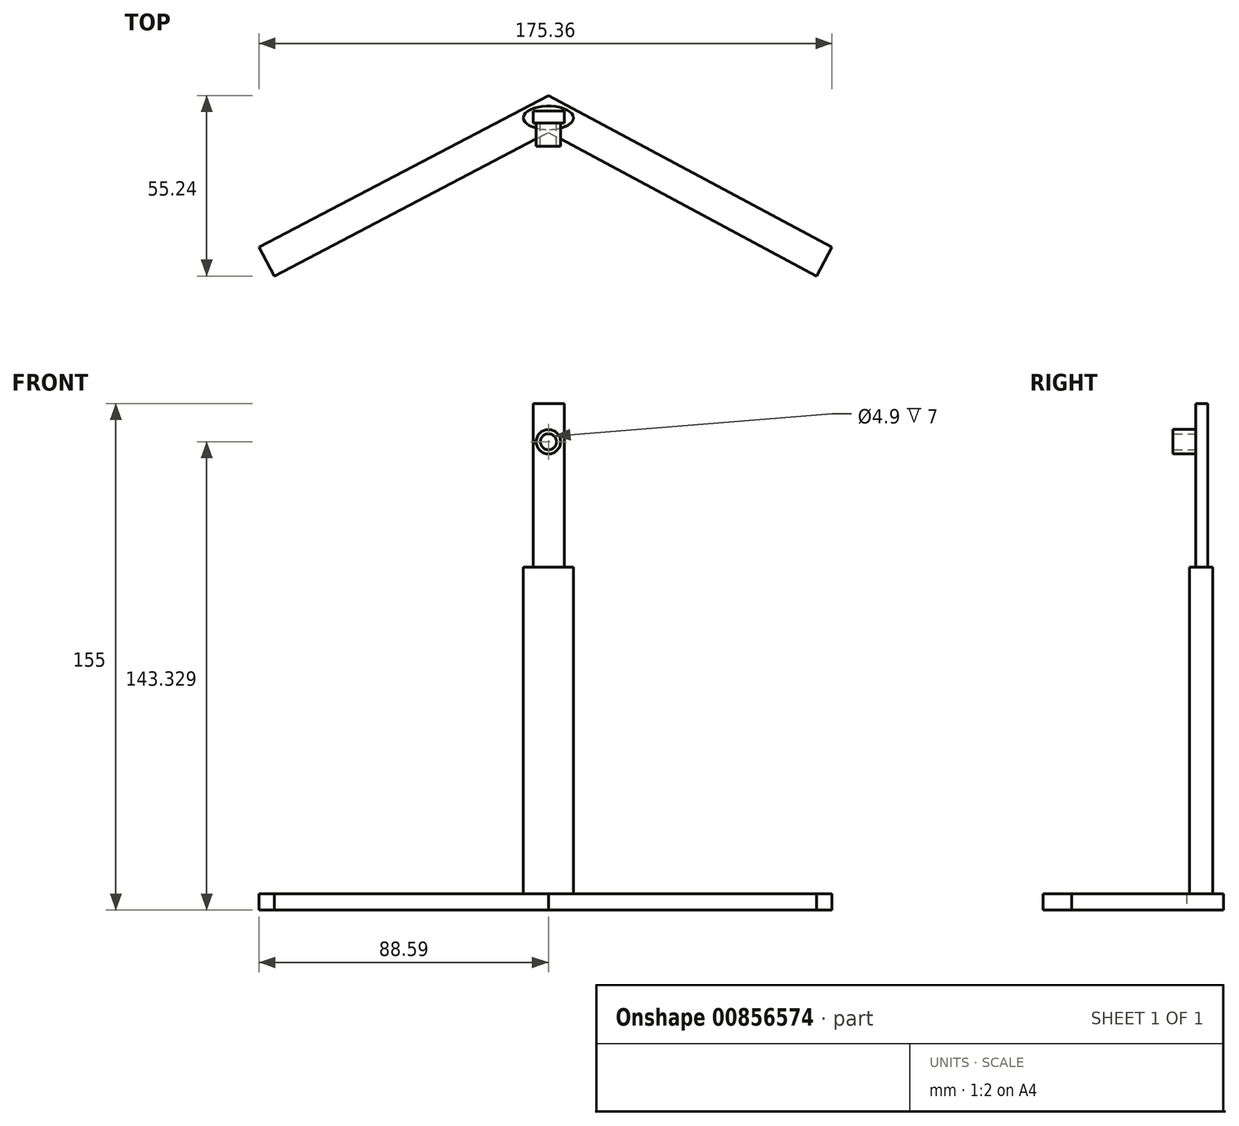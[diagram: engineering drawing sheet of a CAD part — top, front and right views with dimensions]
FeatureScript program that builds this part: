
annotation { "Feature Type Name" : "Feature", "Feature Type Description" : "" }
export const myFeature = defineFeature(function(context is Context, id is Id, definition is map)
    precondition{}
    {
        {
            var Q0;
            Q0=qCreatedBy(makeId("Top.planeOp"),FACE);
            var sketch = newSketch(context, id + "F0", { "sketchPlane" : qUnion([Q0])});
            skLineSegment(sketch, "E0", {"start": v(0, 0) * mm, "end": v(-88.6, -46.38) * mm});
            skLineSegment(sketch, "E1", {"start": v(-88.6, -46.38) * mm, "end": v(-83.95, -55.24) * mm});
            skLineSegment(sketch, "E2", {"start": v(-83.95, -55.24) * mm, "end": v(0, -11.29) * mm});
            skLineSegment(sketch, "E3", {"start": v(0, -11.29) * mm, "end": v(82.05, -55.24) * mm});
            skLineSegment(sketch, "E4", {"start": v(82.05, -55.24) * mm, "end": v(86.77, -46.43) * mm});
            skLineSegment(sketch, "E5", {"start": v(86.77, -46.43) * mm, "end": v(0, 0) * mm});
            skSolve(sketch);
        }
        {
            var Q0;
            Q0=makeQuery(id+"F0.imprint","IMPRINT",FACE,{"disambiguationData":[TD([[makeQuery(id+"F0.imprint","IMPRINT",EDGE,{"derivedFrom":sQuery(id+"F0.wireOp",EDGE,"E0")}),1.0]])]});
            extrude(context, id + "F1", {"entities" : qUnion([Q0]), "depth" : 5 * mm, "offsetDistance" : 25 * mm});
        }
        {
            var Q0;
            Q0=makeQuery(id+"F1.opExtrude","CAP_FACE",FACE,{"disambiguationData":[OSD([sQuery(id+"F0.wireOp",EDGE,"E0"),sQuery(id+"F0.wireOp",EDGE,"E1"),sQuery(id+"F0.wireOp",EDGE,"E2"),sQuery(id+"F0.wireOp",EDGE,"E3"),sQuery(id+"F0.wireOp",EDGE,"E4"),sQuery(id+"F0.wireOp",EDGE,"E5")])],"isStart":false});
            var sketch = newSketch(context, id + "F2", { "sketchPlane" : qUnion([Q0])});
            skEllipse(sketch, "E6", {"center": v(0, -6.81) * mm, "majorRadius": 7.66 * mm, "minorRadius": 3.6 * mm, "majorAxis": v(1, 0)});
            skSolve(sketch);
        }
        {
            var Q0;
            Q0=makeQuery(id+"F2.imprint","IMPRINT",FACE,{"disambiguationData":[TD([[makeQuery(id+"F2.imprint","IMPRINT",EDGE,{"derivedFrom":sQuery(id+"F2.wireOp",EDGE,"E6")}),1.0]])]});
            extrude(context, id + "F3", {"entities" : qUnion([Q0]), "operationType" : NewBodyOperationType.ADD, "depth" : 100 * mm, "offsetDistance" : 25 * mm});
        }
        {
            var Q0;
            Q0=makeQuery(id+"F3.opExtrude","CAP_FACE",FACE,{"disambiguationData":[OSD([sQuery(id+"F2.wireOp",EDGE,"E6")])],"isStart":false});
            var sketch = newSketch(context, id + "F4", { "sketchPlane" : qUnion([Q0])});
            skLineSegment(sketch, "E7.bottom", {"start": v(-4.7, -4.72) * mm, "end": v(4.82, -4.72) * mm});
            skLineSegment(sketch, "E7.top", {"start": v(-4.7, -8.46) * mm, "end": v(4.82, -8.46) * mm});
            skLineSegment(sketch, "E7.left", {"start": v(-4.7, -4.72) * mm, "end": v(-4.7, -8.46) * mm});
            skLineSegment(sketch, "E7.right", {"start": v(4.82, -4.72) * mm, "end": v(4.82, -8.46) * mm});
            skSolve(sketch);
        }
        {
            var Q0;
            Q0=makeQuery(id+"F4.imprint","IMPRINT",FACE,{"disambiguationData":[TD([[makeQuery(id+"F4.imprint","IMPRINT",EDGE,{"derivedFrom":sQuery(id+"F4.wireOp",EDGE,"E7.bottom")}),-1.0]])]});
            extrude(context, id + "F5", {"entities" : qUnion([Q0]), "operationType" : NewBodyOperationType.ADD, "depth" : 50 * mm, "offsetDistance" : 25 * mm});
        }
        {
            var Q0;
            Q0=makeQuery(id+"F5.opExtrude","SWEPT_FACE",FACE,{"disambiguationData":[OSD([sQuery(id+"F4.wireOp",EDGE,"E7.top")])]});
            var sketch = newSketch(context, id + "F6", { "sketchPlane" : qUnion([Q0])});
            skCircle(sketch, "E8", {"center": v(0, 143.33) * mm, "radius": 3.73 * mm});
            skCircle(sketch, "E9", {"center": v(0, 143.33) * mm, "radius": 2.45 * mm});
            skSolve(sketch);
        }
        {
            var Q0;
            Q0=makeQuery(id+"F6.imprint","IMPRINT",FACE,{"disambiguationData":[TD([[makeQuery(id+"F6.imprint","IMPRINT",EDGE,{"derivedFrom":sQuery(id+"F6.wireOp",EDGE,"E8")}),1.0]])]});
            extrude(context, id + "F7", {"entities" : qUnion([Q0]), "depth" : 7 * mm, "offsetDistance" : 25 * mm});
        }
    });
